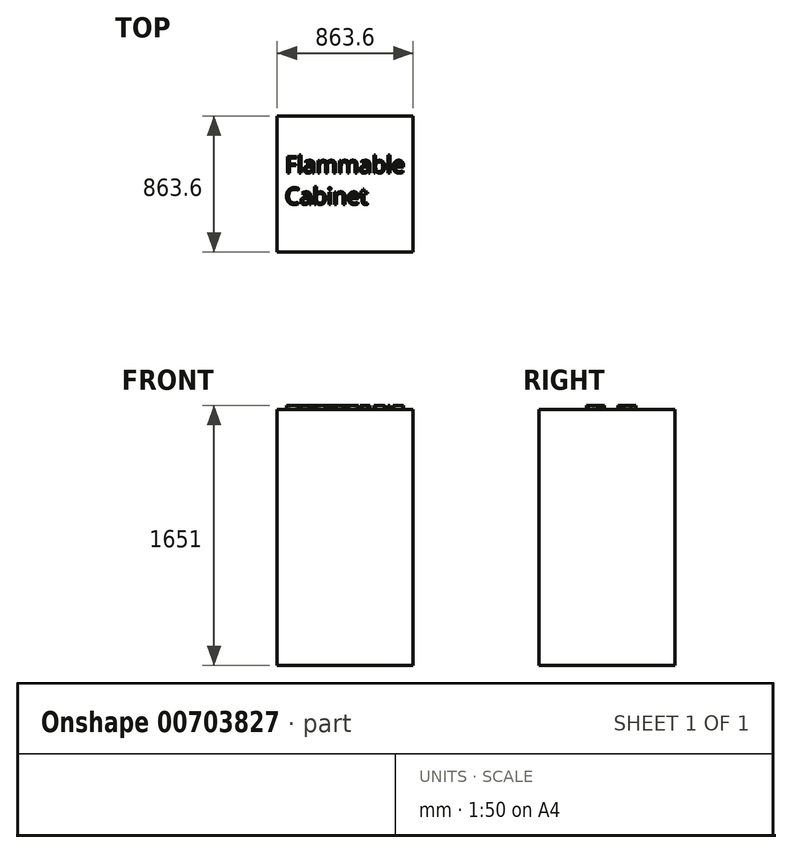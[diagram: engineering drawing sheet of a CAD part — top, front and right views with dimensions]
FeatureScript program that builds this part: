
annotation { "Feature Type Name" : "Feature", "Feature Type Description" : "" }
export const myFeature = defineFeature(function(context is Context, id is Id, definition is map)
    precondition{}
    {
        {
            var Q0;
            Q0=qCreatedBy(makeId("Top.planeOp"),FACE);
            var sketch = newSketch(context, id + "F0", { "sketchPlane" : qUnion([Q0])});
            skLineSegment(sketch, "E0.bottom", {"start": v(431.8, -431.8) * mm, "end": v(-431.8, -431.8) * mm});
            skLineSegment(sketch, "E0.top", {"start": v(431.8, 431.8) * mm, "end": v(-431.8, 431.8) * mm});
            skLineSegment(sketch, "E0.left", {"start": v(431.8, -431.8) * mm, "end": v(431.8, 431.8) * mm});
            skLineSegment(sketch, "E0.right", {"start": v(-431.8, -431.8) * mm, "end": v(-431.8, 431.8) * mm});
            skPoint(sketch, "E0.middle", {"position": v(0, 0) * mm});
            skSolve(sketch);
        }
        {
            var Q0;
            Q0 = qSketchRegion(id + "F0", true);
            extrude(context, id + "F1", {"entities" : qUnion([Q0]), "depth" : 1625.6 * mm, "offsetDistance" : 25.4 * mm});
        }
        {
            var Q0;
            Q0=makeQuery(id+"F1.opExtrude","CAP_FACE",FACE,{"disambiguationData":[OSD([sQuery(id+"F0.wireOp",EDGE,"E0.bottom"),sQuery(id+"F0.wireOp",EDGE,"E0.top"),sQuery(id+"F0.wireOp",EDGE,"E0.left"),sQuery(id+"F0.wireOp",EDGE,"E0.right")])],"isStart":false});
            var sketch = newSketch(context, id + "F2", { "sketchPlane" : qUnion([Q0])});
            skText(sketch, "E1", { "text": "Flammable\nCabinet", "fontName": "OpenSans-Regular.ttf"});
            const initialGuessF2  = {"E1": [-0.381, 0.07098, 1, 0, 0.1059]};
            skSetInitialGuess(sketch, initialGuessF2);
            skSolve(sketch);
        }
        {
            var Q0;
            Q0 = qSketchRegion(id + "F2", true);
            extrude(context, id + "F3", {"entities" : qUnion([Q0]), "operationType" : NewBodyOperationType.ADD, "depth" : 25.4 * mm, "offsetDistance" : 25.4 * mm});
        }
    });
